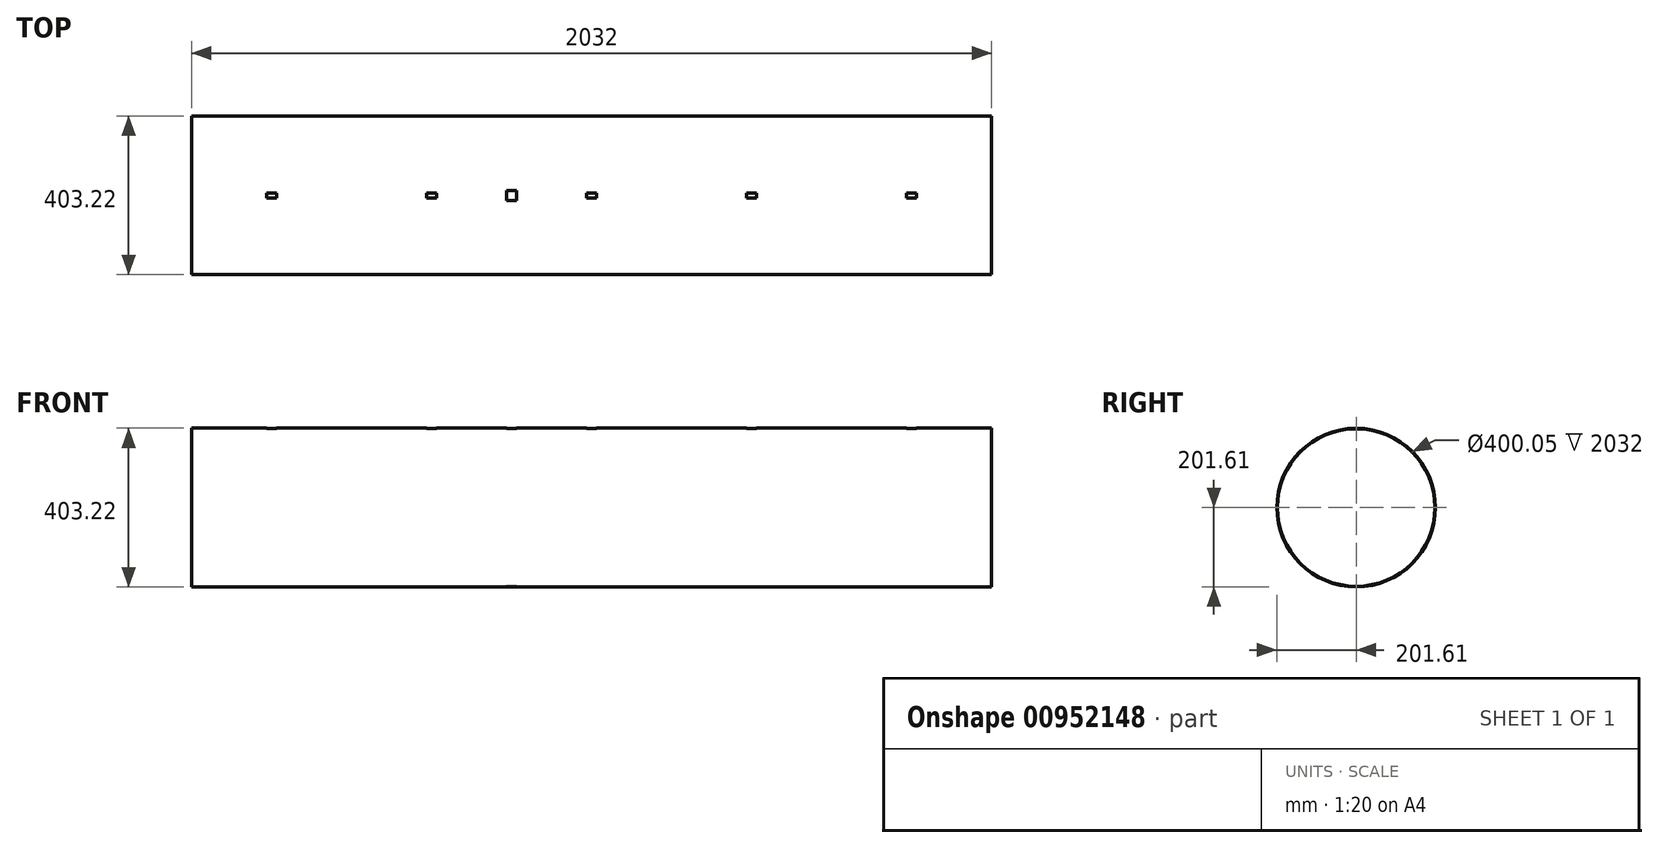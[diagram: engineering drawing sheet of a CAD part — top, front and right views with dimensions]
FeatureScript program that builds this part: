
annotation { "Feature Type Name" : "Feature", "Feature Type Description" : "" }
export const myFeature = defineFeature(function(context is Context, id is Id, definition is map)
    precondition{}
    {
        {
            var Q0;
            Q0=qCreatedBy(makeId("Right.planeOp"),FACE);
            var sketch = newSketch(context, id + "F0", { "sketchPlane" : qUnion([Q0])});
            skCircle(sketch, "E0", {"center": v(0, 0) * mm, "radius": 201.61 * mm});
            skCircle(sketch, "E1", {"center": v(0, 0) * mm, "radius": 200.03 * mm});
            skSolve(sketch);
        }
        {
            var Q0;
            Q0=makeQuery(id+"F0.imprint","IMPRINT",FACE,{"disambiguationData":[TD([[makeQuery(id+"F0.imprint","IMPRINT",EDGE,{"derivedFrom":sQuery(id+"F0.wireOp",EDGE,"E0")}),1.0]])]});
            extrude(context, id + "F1", {"entities" : qUnion([Q0]), "depth" : 2032 * mm, "offsetDistance" : 25.4 * mm});
        }
        {
            var Q0;
            Q0=qCreatedBy(makeId("Top.planeOp"),FACE);
            var sketch = newSketch(context, id + "F2", { "sketchPlane" : qUnion([Q0])});
            skLineSegment(sketch, "E2", {"start": v(0, 0) * mm, "end": v(406.4, 0) * mm, "construction": true});
            skLineSegment(sketch, "E3", {"start": v(406.4, 0) * mm, "end": v(812.8, 0) * mm, "construction": true});
            skLineSegment(sketch, "E4", {"start": v(812.8, 0) * mm, "end": v(1219.2, 0) * mm, "construction": true});
            skLineSegment(sketch, "E5", {"start": v(1219.2, 0) * mm, "end": v(1625.6, 0) * mm, "construction": true});
            skLineSegment(sketch, "E6", {"start": v(1625.6, 0) * mm, "end": v(2032, 0) * mm, "construction": true});
            skLineSegment(sketch, "E7.bottom", {"start": v(825.5, -12.7) * mm, "end": v(800.1, -12.7) * mm});
            skLineSegment(sketch, "E7.top", {"start": v(825.5, 12.7) * mm, "end": v(800.1, 12.7) * mm});
            skLineSegment(sketch, "E7.left", {"start": v(825.5, -12.7) * mm, "end": v(825.5, 12.7) * mm});
            skLineSegment(sketch, "E7.right", {"start": v(800.1, -12.7) * mm, "end": v(800.1, 12.7) * mm});
            skPoint(sketch, "E7.middle", {"position": v(812.8, 0) * mm});
            skSolve(sketch);
        }
        {
            var Q0;
            Q0=makeQuery(id+"F2.imprint","IMPRINT",FACE,{"disambiguationData":[TD([[makeQuery(id+"F2.imprint","IMPRINT",EDGE,{"derivedFrom":sQuery(id+"F2.wireOp",EDGE,"E7.bottom")}),-1.0]])]});
            extrude(context, id + "F3", {"entities" : qUnion([Q0]), "depth" : 508 * mm, "offsetDistance" : 25.4 * mm});
        }
        {
            var Q0;
            Q0=makeQuery(id+"F3.opExtrude","CAP_FACE",FACE,{"disambiguationData":[OSD([sQuery(id+"F2.wireOp",EDGE,"E7.bottom"),sQuery(id+"F2.wireOp",EDGE,"E7.top"),sQuery(id+"F2.wireOp",EDGE,"E7.left"),sQuery(id+"F2.wireOp",EDGE,"E7.right")])],"isStart":false});
            extrude(context, id + "F4", {"entities" : qUnion([Q0]), "operationType" : NewBodyOperationType.REMOVE, "endBound" : BoundingType.THROUGH_ALL, "depth" : 1016 * mm, "offsetDistance" : 25.4 * mm, "hasSecondDirection" : true, "secondDirectionBound" : SecondDirectionBoundingType.THROUGH_ALL, "secondDirectionOppositeDirection" : true, "secondDirectionDepth" : 25.4 * mm});
        }
        {
            var Q0;
            Q0=qCreatedBy(makeId("Top.planeOp"),FACE);
            var sketch = newSketch(context, id + "F5", { "sketchPlane" : qUnion([Q0])});
            skLineSegment(sketch, "E8", {"start": v(203.2, 203.2) * mm, "end": v(203.2, -203.2) * mm, "construction": true});
            skLineSegment(sketch, "E9.bottom", {"start": v(190.5, 6.35) * mm, "end": v(215.9, 6.35) * mm});
            skLineSegment(sketch, "E9.top", {"start": v(190.5, -6.35) * mm, "end": v(215.9, -6.35) * mm});
            skLineSegment(sketch, "E9.left", {"start": v(190.5, 6.35) * mm, "end": v(190.5, -6.35) * mm});
            skLineSegment(sketch, "E9.right", {"start": v(215.9, 6.35) * mm, "end": v(215.9, -6.35) * mm});
            skLineSegment(sketch, "E10", {"start": v(609.6, 284.16) * mm, "end": v(609.6, -122.24) * mm, "construction": true});
            skLineSegment(sketch, "E11", {"start": v(1016, 109.34) * mm, "end": v(1016, -122.04) * mm, "construction": true});
            skLineSegment(sketch, "E12", {"start": v(1422.4, 129.67) * mm, "end": v(1422.4, -173.86) * mm, "construction": true});
            skLineSegment(sketch, "E13", {"start": v(1828.8, 150.24) * mm, "end": v(1828.8, -167.52) * mm, "construction": true});
            skLineSegment(sketch, "E14.bottom", {"start": v(596.9, 6.35) * mm, "end": v(622.3, 6.35) * mm});
            skLineSegment(sketch, "E14.top", {"start": v(596.9, -6.35) * mm, "end": v(622.3, -6.35) * mm});
            skLineSegment(sketch, "E14.left", {"start": v(596.9, 6.35) * mm, "end": v(596.9, -6.35) * mm});
            skLineSegment(sketch, "E14.right", {"start": v(622.3, 6.35) * mm, "end": v(622.3, -6.35) * mm});
            skPoint(sketch, "E15.oppositeSnap0", {"position": v(1016, -6.35) * mm});
            skLineSegment(sketch, "E15.bottom", {"start": v(1003.3, 6.35) * mm, "end": v(1028.7, 6.35) * mm});
            skLineSegment(sketch, "E15.top", {"start": v(1003.3, -6.35) * mm, "end": v(1028.7, -6.35) * mm});
            skLineSegment(sketch, "E15.left", {"start": v(1003.3, 6.35) * mm, "end": v(1003.3, -6.35) * mm});
            skLineSegment(sketch, "E15.right", {"start": v(1028.7, 6.35) * mm, "end": v(1028.7, -6.35) * mm});
            skLineSegment(sketch, "E16.bottom", {"start": v(1409.7, 6.35) * mm, "end": v(1435.1, 6.35) * mm});
            skLineSegment(sketch, "E16.top", {"start": v(1409.7, -6.35) * mm, "end": v(1435.1, -6.35) * mm});
            skLineSegment(sketch, "E16.left", {"start": v(1409.7, 6.35) * mm, "end": v(1409.7, -6.35) * mm});
            skLineSegment(sketch, "E16.right", {"start": v(1435.1, 6.35) * mm, "end": v(1435.1, -6.35) * mm});
            skLineSegment(sketch, "E17.bottom", {"start": v(1816.1, 6.35) * mm, "end": v(1841.5, 6.35) * mm});
            skLineSegment(sketch, "E17.top", {"start": v(1816.1, -6.35) * mm, "end": v(1841.5, -6.35) * mm});
            skLineSegment(sketch, "E17.left", {"start": v(1816.1, 6.35) * mm, "end": v(1816.1, -6.35) * mm});
            skLineSegment(sketch, "E17.right", {"start": v(1841.5, 6.35) * mm, "end": v(1841.5, -6.35) * mm});
            skSolve(sketch);
        }
        {
            var Q0;
            Q0=makeQuery(id+"F5.imprint","IMPRINT",FACE,{"disambiguationData":[TD([[makeQuery(id+"F5.imprint","IMPRINT",EDGE,{"derivedFrom":sQuery(id+"F5.wireOp",EDGE,"E9.bottom")}),-1.0]])]});
            var Q1;
            Q1=makeQuery(id+"F5.imprint","IMPRINT",FACE,{"disambiguationData":[TD([[makeQuery(id+"F5.imprint","IMPRINT",EDGE,{"derivedFrom":sQuery(id+"F5.wireOp",EDGE,"E14.bottom")}),-1.0]])]});
            var Q2;
            Q2=makeQuery(id+"F5.imprint","IMPRINT",FACE,{"disambiguationData":[TD([[makeQuery(id+"F5.imprint","IMPRINT",EDGE,{"derivedFrom":sQuery(id+"F5.wireOp",EDGE,"E15.bottom")}),-1.0]])]});
            var Q3;
            Q3=makeQuery(id+"F5.imprint","IMPRINT",FACE,{"disambiguationData":[TD([[makeQuery(id+"F5.imprint","IMPRINT",EDGE,{"derivedFrom":sQuery(id+"F5.wireOp",EDGE,"E16.bottom")}),-1.0]])]});
            var Q4;
            Q4=makeQuery(id+"F5.imprint","IMPRINT",FACE,{"disambiguationData":[TD([[makeQuery(id+"F5.imprint","IMPRINT",EDGE,{"derivedFrom":sQuery(id+"F5.wireOp",EDGE,"E17.bottom")}),-1.0]])]});
            extrude(context, id + "F6", {"entities" : qUnion([Q0, Q1, Q2, Q3, Q4]), "operationType" : NewBodyOperationType.REMOVE, "endBound" : BoundingType.THROUGH_ALL, "depth" : 25.4 * mm, "offsetDistance" : 25.4 * mm, "hasSecondDirection" : true, "secondDirectionBound" : SecondDirectionBoundingType.THROUGH_ALL, "secondDirectionOppositeDirection" : true, "secondDirectionDepth" : 25.4 * mm});
        }
    });
